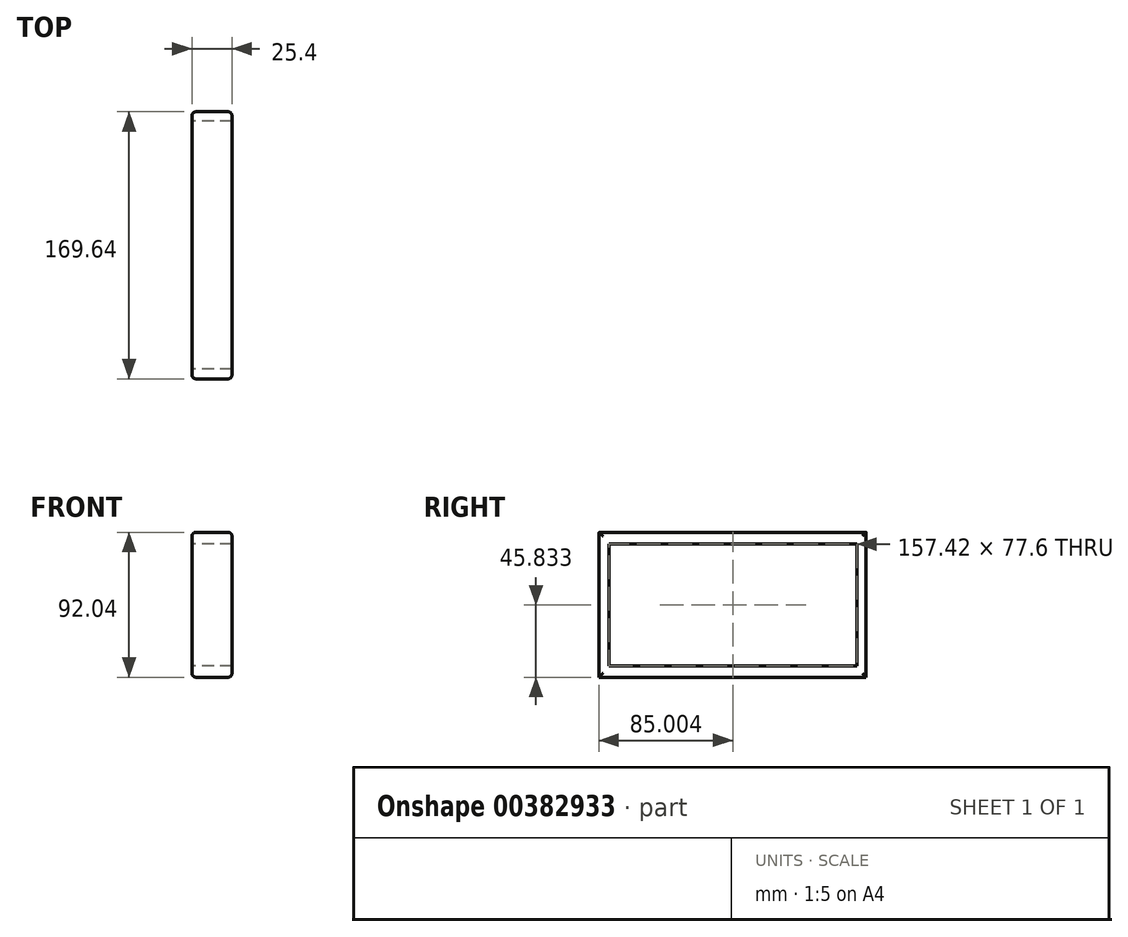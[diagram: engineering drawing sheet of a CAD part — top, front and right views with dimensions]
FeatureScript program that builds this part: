
annotation { "Feature Type Name" : "Feature", "Feature Type Description" : "" }
export const myFeature = defineFeature(function(context is Context, id is Id, definition is map)
    precondition{}
    {
        {
            var Q0;
            Q0=qCreatedBy(makeId("Right.planeOp"),FACE);
            var sketch = newSketch(context, id + "F0", { "sketchPlane" : qUnion([Q0])});
            skLineSegment(sketch, "E0.bottom", {"start": v(-84.98, 44.84) * mm, "end": v(84.66, 44.84) * mm});
            skLineSegment(sketch, "E0.top", {"start": v(-84.98, -47.2) * mm, "end": v(84.66, -47.2) * mm});
            skLineSegment(sketch, "E0.left", {"start": v(-84.98, 44.84) * mm, "end": v(-84.98, -47.2) * mm});
            skLineSegment(sketch, "E0.right", {"start": v(84.66, 44.84) * mm, "end": v(84.66, -47.2) * mm});
            skLineSegment(sketch, "E1.bottom", {"start": v(-78.68, 37.43) * mm, "end": v(78.73, 37.43) * mm});
            skLineSegment(sketch, "E1.top", {"start": v(-78.68, -40.17) * mm, "end": v(78.73, -40.17) * mm});
            skLineSegment(sketch, "E1.left", {"start": v(-78.68, 37.43) * mm, "end": v(-78.68, -40.17) * mm});
            skLineSegment(sketch, "E1.right", {"start": v(78.73, 37.43) * mm, "end": v(78.73, -40.17) * mm});
            skSolve(sketch);
        }
        {
            var Q0;
            Q0 = qSketchRegion(id + "F0", true);
            extrude(context, id + "F1", {"entities" : qUnion([Q0]), "depth" : 25.4 * mm});
        }
        {
            var Q0;
            Q0=makeQuery(id+"F1.opExtrude","CAP_EDGE",EDGE,{"disambiguationData":[OSD([sQuery(id+"F0.wireOp",EDGE,"E0.top")])],"isStart":false});
            var Q1;
            Q1=makeQuery(id+"F1.opExtrude","CAP_EDGE",EDGE,{"disambiguationData":[OSD([sQuery(id+"F0.wireOp",EDGE,"E0.left")])],"isStart":false});
            var Q2;
            Q2=makeQuery(id+"F1.opExtrude","CAP_EDGE",EDGE,{"disambiguationData":[OSD([sQuery(id+"F0.wireOp",EDGE,"E0.bottom")])],"isStart":false});
            var Q3;
            Q3=makeQuery(id+"F1.opExtrude","CAP_EDGE",EDGE,{"disambiguationData":[OSD([sQuery(id+"F0.wireOp",EDGE,"E0.right")])],"isStart":false});
            fillet(context, id + "F2", {"entities" : qUnion([Q0, Q1, Q2, Q3]), "radius" : 2.45 * mm, "tangentPropagation" : true, "allowEdgeOverflow" : false});
        }
        {
            var Q0;
            Q0=makeQuery(id+"F1.opExtrude","CAP_EDGE",EDGE,{"disambiguationData":[OSD([sQuery(id+"F0.wireOp",EDGE,"E0.right")])],"isStart":true});
            var Q1;
            Q1=makeQuery(id+"F1.opExtrude","CAP_EDGE",EDGE,{"disambiguationData":[OSD([sQuery(id+"F0.wireOp",EDGE,"E0.bottom")])],"isStart":true});
            var Q2;
            Q2=makeQuery(id+"F1.opExtrude","CAP_EDGE",EDGE,{"disambiguationData":[OSD([sQuery(id+"F0.wireOp",EDGE,"E0.top")])],"isStart":true});
            var Q3;
            Q3=makeQuery(id+"F1.opExtrude","CAP_EDGE",EDGE,{"disambiguationData":[OSD([sQuery(id+"F0.wireOp",EDGE,"E0.left")])],"isStart":true});
            fillet(context, id + "F3", {"entities" : qUnion([Q0, Q1, Q2, Q3]), "radius" : 2.46 * mm, "tangentPropagation" : true, "allowEdgeOverflow" : false});
        }
    });
